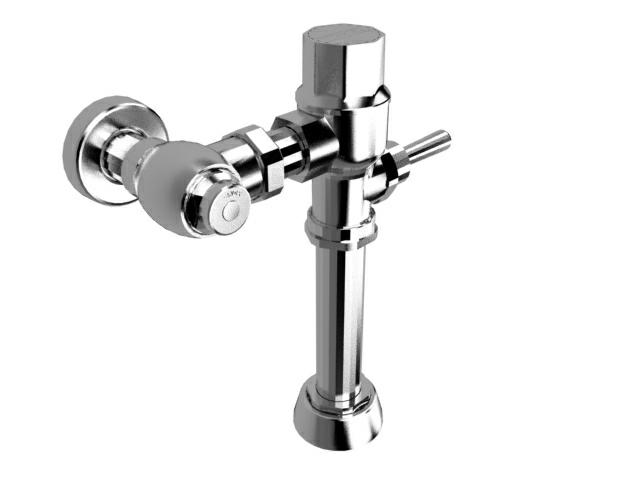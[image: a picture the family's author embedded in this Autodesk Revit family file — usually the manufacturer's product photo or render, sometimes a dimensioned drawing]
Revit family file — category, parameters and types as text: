
# Revit family: Fluxómetros 110-WC-4.8
name_source: partatom
category: Generic Models
revit_build: Autodesk Revit 2015 (Build: 20140223_1515(x64)
units: mm (PartAtom-declared; Revit-internal decimal feet)

## types (1)
- 110-WC-4.8
    Compliance = NOM-005-CONAGUA-1996
    Connection = 1"
    Default Elevation = 1 "
    Description = Fluxómetro para W. C. de manija con recubrimiento antibacterial. Entrada superior para spud de 32 mm ó 38 mm. Descarga de 4,8 l por accionamiento. Camisa recortable. Conexión izquierda o derecha. Niple recto Ø 32 mm x 9" de largo
    Manufacturer = HELVEX S.A. DE C.V.
    Material = Brass Chromed
    Max. Working Pressure = 85.3 psi
    Min. Working Pressure = 14.2 psi
    Model = 110-WC-4.8
    Note = La tubería de alimentación debe tener un Ø 32 mm mínimo y debe conectarse una reducción de campana de 32 mm - 25 mm a la llave de retención.
    Type Comments = Fluxómetro para W. C. de manija
    Type Image = 110-WC-4.8.jpg
    URL = http://www.helvex.com.mx

## geometry (parser evidence)
native form markers: Sweep x5
no freeform markers — native parametric forms only
